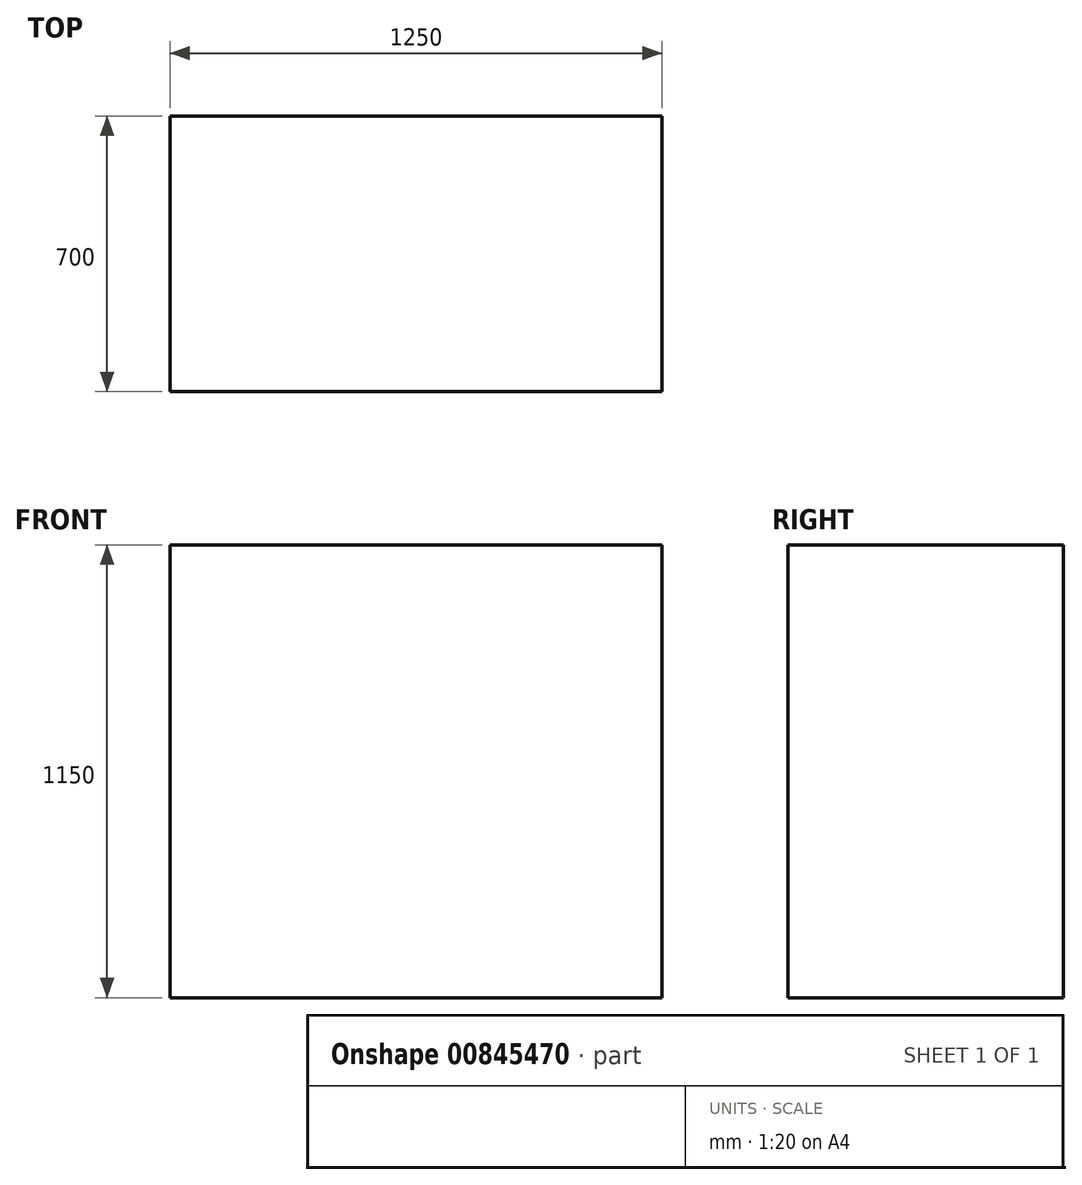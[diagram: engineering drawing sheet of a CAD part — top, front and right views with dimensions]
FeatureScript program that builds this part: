
annotation { "Feature Type Name" : "Feature", "Feature Type Description" : "" }
export const myFeature = defineFeature(function(context is Context, id is Id, definition is map)
    precondition{}
    {
        {
            var Q0;
            Q0=qCreatedBy(makeId("Top.planeOp"),FACE);
            var sketch = newSketch(context, id + "F0", { "sketchPlane" : qUnion([Q0])});
            skLineSegment(sketch, "E0.bottom", {"start": v(625, -350) * mm, "end": v(-625, -350) * mm});
            skLineSegment(sketch, "E0.top", {"start": v(625, 350) * mm, "end": v(-625, 350) * mm});
            skLineSegment(sketch, "E0.left", {"start": v(625, -350) * mm, "end": v(625, 350) * mm});
            skLineSegment(sketch, "E0.right", {"start": v(-625, -350) * mm, "end": v(-625, 350) * mm});
            skPoint(sketch, "E0.middle", {"position": v(0, 0) * mm});
            skSolve(sketch);
        }
        {
            var Q0;
            Q0 = qSketchRegion(id + "F0", true);
            extrude(context, id + "F1", {"entities" : qUnion([Q0]), "depth" : 1150 * mm, "offsetDistance" : 25 * mm});
        }
    });
